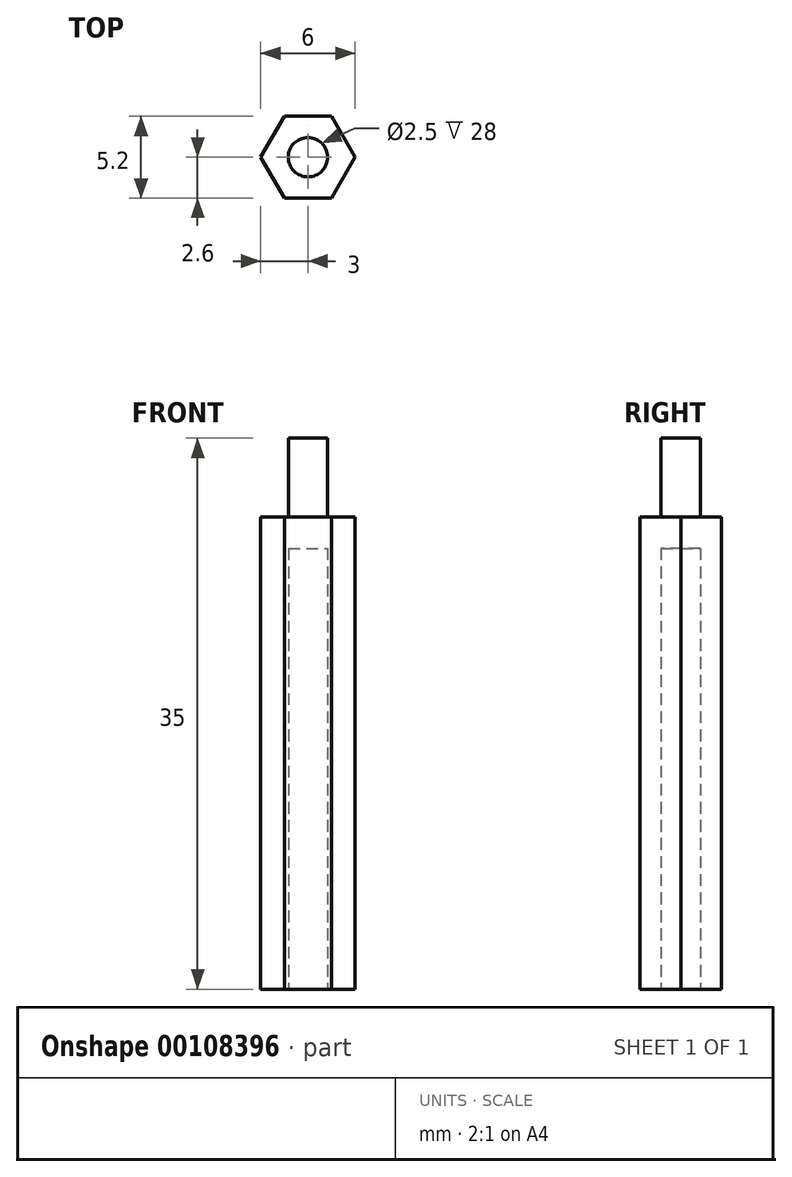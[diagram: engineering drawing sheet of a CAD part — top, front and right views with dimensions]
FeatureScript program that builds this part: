
annotation { "Feature Type Name" : "Feature", "Feature Type Description" : "" }
export const myFeature = defineFeature(function(context is Context, id is Id, definition is map)
    precondition{}
    {
        {
            var Q0;
            Q0=qCreatedBy(makeId("Top.planeOp"),FACE);
            var sketch = newSketch(context, id + "F0", { "sketchPlane" : qUnion([Q0])});
            skCircle(sketch, "E0.cCircle", {"center": v(0, 0) * mm, "radius": 2.6 * mm, "construction": true});
            skLineSegment(sketch, "E0.0", {"start": v(-1.5, 2.6) * mm, "end": v(1.5, 2.6) * mm});
            skLineSegment(sketch, "E0.1", {"start": v(1.5, 2.6) * mm, "end": v(3, 0) * mm});
            skLineSegment(sketch, "E0.2", {"start": v(3, 0) * mm, "end": v(1.5, -2.6) * mm});
            skLineSegment(sketch, "E0.3", {"start": v(1.5, -2.6) * mm, "end": v(-1.5, -2.6) * mm});
            skLineSegment(sketch, "E0.4", {"start": v(-1.5, -2.6) * mm, "end": v(-3, 0) * mm});
            skLineSegment(sketch, "E0.5", {"start": v(-3, 0) * mm, "end": v(-1.5, 2.6) * mm});
            skPoint(sketch, "E0.0.midPoint", {"position": v(0, 2.6) * mm});
            skCircle(sketch, "E1", {"center": v(0, 0) * mm, "radius": 1.25 * mm});
            skSolve(sketch);
        }
        {
            var Q0;
            Q0=makeQuery(id+"F0.imprint","IMPRINT",FACE,{"disambiguationData":[TD([[makeQuery(id+"F0.imprint","IMPRINT",EDGE,{"derivedFrom":sQuery(id+"F0.wireOp",EDGE,"E0.0")}),-1.0]])]});
            var Q1;
            Q1=makeQuery(id+"F0.imprint","IMPRINT",FACE,{"disambiguationData":[TD([[makeQuery(id+"F0.imprint","IMPRINT",EDGE,{"derivedFrom":sQuery(id+"F0.wireOp",EDGE,"30d041f5-1b89-4233-92af-d11f27702ac6.0")}),-1.0]])]});
            extrude(context, id + "F1", {"entities" : qUnion([Q0, Q1]), "depth" : 30 * mm});
        }
        {
            var Q0;
            Q0=makeQuery(id+"F0.imprint","IMPRINT",FACE,{"disambiguationData":[TD([[makeQuery(id+"F0.imprint","IMPRINT",EDGE,{"derivedFrom":sQuery(id+"F0.wireOp",EDGE,"R5qQFAYa-yBxM-nc6b-MVFJ-eDeeQs0Jteww")}),1.0]])]});
            var Q1;
            Q1=makeQuery(id+"F0.imprint","IMPRINT",FACE,{"disambiguationData":[TD([[makeQuery(id+"F0.imprint","IMPRINT",EDGE,{"derivedFrom":sQuery(id+"F0.wireOp",EDGE,"E1")}),1.0]])]});
            extrude(context, id + "F2", {"entities" : qUnion([Q0, Q1]), "operationType" : NewBodyOperationType.ADD, "depth" : 35 * mm});
        }
        {
            var Q0;
            {var subQ0=sQuery(id+"F0.wireOp",EDGE,"E1");Q0=makeQuery(id+"F2.boolean.opBoolean","MERGE",FACE,{"derivedFrom":[makeQuery(id+"F1.opExtrude","CAP_FACE",FACE,{"disambiguationData":[OSD([sQuery(id+"F0.wireOp",EDGE,"E0.0"),sQuery(id+"F0.wireOp",EDGE,"E0.1"),sQuery(id+"F0.wireOp",EDGE,"E0.2"),sQuery(id+"F0.wireOp",EDGE,"E0.3"),sQuery(id+"F0.wireOp",EDGE,"E0.4"),sQuery(id+"F0.wireOp",EDGE,"E0.5"),subQ0])],"isStart":true}),makeQuery(id+"F2.opExtrude","CAP_FACE",FACE,{"disambiguationData":[OSD([subQ0])],"isStart":true})]});}
            var sketch = newSketch(context, id + "F3", { "sketchPlane" : qUnion([Q0])});
            skCircle(sketch, "E2", {"center": v(0, 0) * mm, "radius": 1.25 * mm});
            skSolve(sketch);
        }
        {
            var Q0;
            Q0 = qSketchRegion(id + "F3", true);
            extrude(context, id + "F4", {"entities" : qUnion([Q0]), "operationType" : NewBodyOperationType.REMOVE, "oppositeDirection" : true, "depth" : 28 * mm});
        }
    });
